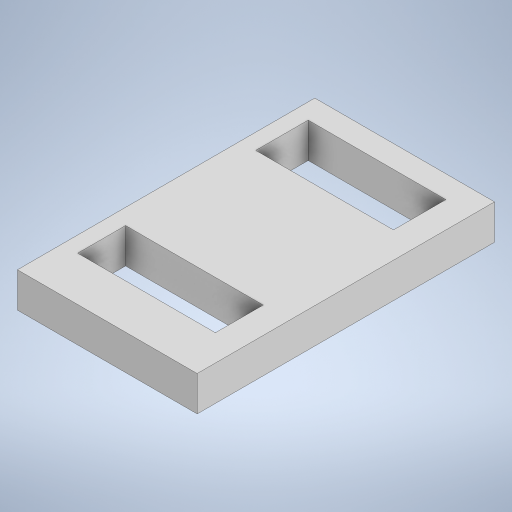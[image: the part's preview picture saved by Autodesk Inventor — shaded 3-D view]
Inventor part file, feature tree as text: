
AUTODESK INVENTOR PART (.ipt)
format: ipt  version: 2024.2 (Build 282272000, 272)  size: 289,792 bytes
history: native  units: mm
features: extrude x2, sketch x2, other x1
ambient origin geometry x8: Origin, YZ Plane, XZ Plane, XY Plane, X Axis, Y Axis, Z Axis, Center Point
bodies: Body1 (feature_tree)
feature tree (5):
  other  "Твердое тело1"
  extrude  "Выдавливание1"  Depth=2.0mm TaperAngle=0.0deg
  extrude  "Выдавливание2"  Depth=17.0mm
  sketch  "Эскиз1"
  sketch  "Эскиз3"
